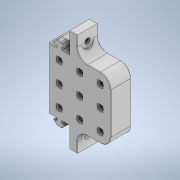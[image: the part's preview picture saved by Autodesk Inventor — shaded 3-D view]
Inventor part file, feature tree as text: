
AUTODESK INVENTOR PART (.ipt)
format: ipt  version: 2020 (Build 240168000, 168)  size: 700,416 bytes
history: native  units: in
note: dims shown in document units (in); Inventor stores cm internally (conversion verified against a paired STEP export)
features: reference x53, extrude x9, sketch x9, other x6, fillet x3, chamfer x1
ambient origin geometry x8: Origin, YZ Plane, XZ Plane, XY Plane, X Axis, Y Axis, Z Axis, Center Point
bodies: Solid1 (feature_tree)
feature tree (81):
  extrude  "Extrusion1"  Depth=0.0098in
  extrude  "Extrusion2"  Depth=0.0098in
  extrude  "Extrusion3"  Depth=1.0in TaperAngle=0.0deg
  extrude  "Extrusion4"  Depth=1.0in
  fillet  "Fillet1"  [1 undecoded]
  fillet  "Fillet2"  Radius=2.0in
  chamfer  "Chamfer1"  [1 undecoded]
  extrude  "Extrusion6"  Depth=0.5in
  extrude  "Extrusion7"  Depth=0.2656in
  extrude  "Extrusion8"  Depth=1.0in TaperAngle=0.0deg
  fillet  "Fillet3"  Radius=0.5in
  extrude  "Extrusion9"  Depth=0.025in TaperAngle=45.0deg
  extrude  "Extrusion10"  Depth=0.125in TaperAngle=0.0deg
  sketch  "Sketch1"  dims[d0=0.0098in d1=0.0098in]
  reference  "Reference1"
  reference  "Reference2"
  reference  "Reference3"
  reference  "Reference4"
  reference  "Reference5"
  reference  "Reference6"
  reference  "Reference7"
  reference  "Reference8"
  reference  "Reference9"
  reference  "Reference10"
  reference  "Reference11"
  reference  "Reference12"
  reference  "Reference13"
  reference  "Reference14"
  reference  "Reference15"
  reference  "Reference16"
  reference  "Reference17"
  reference  "Reference18"
  reference  "Reference19"
  reference  "Reference20"
  reference  "Reference21"
  reference  "Reference22"
  reference  "Reference23"
  reference  "Reference24"
  reference  "Reference25"
  reference  "Reference26"
  reference  "Reference27"
  reference  "Reference28"
  reference  "Reference29"
  reference  "Reference30"
  reference  "Reference31"
  reference  "Reference32"
  reference  "Reference33"
  reference  "Reference34"
  reference  "Reference35"
  reference  "Reference36"
  reference  "Reference37"
  reference  "Reference38"
  reference  "Reference39"
  reference  "Reference40"
  reference  "Reference41"
  reference  "Reference42"
  reference  "Reference43"
  reference  "Reference44"
  reference  "Reference45"
  reference  "Reference46"
  reference  "Reference47"
  reference  "Reference48"
  reference  "Reference49"
  reference  "Reference50"
  reference  "Reference51"
  reference  "Reference52"
  sketch  "Sketch3"  dims[d2=0.0098in d3=0.0098in]
  reference  "Reference53"
  sketch  "Sketch4"  dims[d4=0.9963in d5=1.0in d6=0.0in]
  sketch  "Sketch5"  dims[d7=0.2656in d8=1.0in]
  sketch  "Sketch8"  dims[d9=1.1811in d11=1.0in d12=1.1811in d14=1.0in d17=0.0in d18=0.0in d19=2.0in d20=0.0in d21=0.0in]
  sketch  "Sketch9"  dims[d22=0.375in d23=0.5in]
  sketch  "Sketch10"  dims[d24=0.5in d25=0.2656in]
  sketch  "Sketch11"  dims[d26=0.7874in d28=4.0in d29=0.3937in d31=1.0in d33=1.0in d34=0.0in d38=0.5in]
  sketch  "Sketch12"  dims[d39=0.5in d40=0.025in d41=0.125in d42=45.0deg d43=0.125in d44=0.0in d45=0.6in d46=1.0in d47=0.0in d48=0.6in d49=1.625in d50=0.0in d51=0.0375in d52=1.1811in d54=1.0in d55=1.1811in d57=1.0in d60=0.125in d61=0.0in d62=1.1811in d64=1.0in d65=1.1811in d67=1.0in d70=0.125in d71=0.0in]
  other  "<userpath>\Documents\FRC\2020\ShooterPrototype.iam"
  other  "ShooterPrototype.iam"
  other  "1003-48-CL:3"
  other  "1003-48-CL:4"
  other  "1003-48-CL:1"
  other  "1003-48-CL:2"
note: 2 required parameter values undecoded (feature->parameter linkage not recoverable at this tier; creation-order binding heuristic only, values carry confidence <= 0.55)
